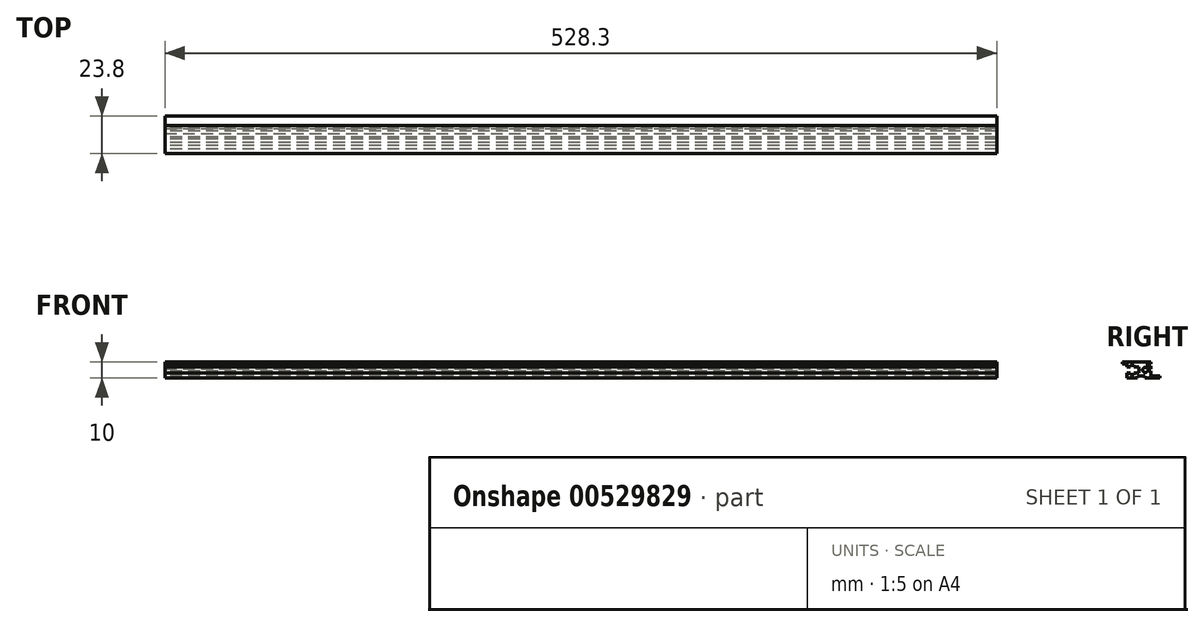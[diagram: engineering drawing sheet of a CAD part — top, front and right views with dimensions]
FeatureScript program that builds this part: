
annotation { "Feature Type Name" : "Feature", "Feature Type Description" : "" }
export const myFeature = defineFeature(function(context is Context, id is Id, definition is map)
    precondition{}
    {
        {
            assignVariable(context, id + "F0", {"name" : "length", "anyValue" : 528.3});
        }
        {
            var Q0;
            Q0=qCreatedBy(makeId("Right.planeOp"),FACE);
            var sketch = newSketch(context, id + "F1", { "sketchPlane" : qUnion([Q0])});
            skLineSegment(sketch, "E0.top", {"start": v(-37.38, 18.75) * mm, "end": v(-34.58, 18.75) * mm});
            skLineSegment(sketch, "E1", {"start": v(-37.38, 19.95) * mm, "end": v(-37.38, 18.75) * mm});
            skLineSegment(sketch, "E2.top", {"start": v(-13.58, 11.15) * mm, "end": v(-19.58, 11.15) * mm});
            skLineSegment(sketch, "E3", {"start": v(-37.38, 19.95) * mm, "end": v(-19.58, 19.95) * mm});
            skLineSegment(sketch, "E4", {"start": v(-13.58, 11.15) * mm, "end": v(-13.58, 9.95) * mm});
            skLineSegment(sketch, "E5.bottom", {"start": v(-19.58, 19.95) * mm, "end": v(-21.58, 19.95) * mm});
            skLineSegment(sketch, "E5.top", {"start": v(-19.58, 18.75) * mm, "end": v(-21.58, 18.75) * mm});
            skLineSegment(sketch, "E5.left", {"start": v(-19.58, 19.95) * mm, "end": v(-19.58, 18.75) * mm});
            skLineSegment(sketch, "E6.bottom", {"start": v(-21.58, 18.75) * mm, "end": v(-19.58, 18.75) * mm});
            skLineSegment(sketch, "E6.top", {"start": v(-21.58, 17.35) * mm, "end": v(-19.58, 17.35) * mm});
            skLineSegment(sketch, "E6.left", {"start": v(-21.58, 18.75) * mm, "end": v(-21.58, 17.35) * mm});
            skLineSegment(sketch, "E7.right", {"start": v(-26.98, 12.95) * mm, "end": v(-26.98, 16.95) * mm});
            skLineSegment(sketch, "E8", {"start": v(-34.58, 18.75) * mm, "end": v(-34.58, 16.95) * mm});
            skLineSegment(sketch, "E9.bottom", {"start": v(-34.58, 12.95) * mm, "end": v(-32.32, 12.95) * mm});
            skLineSegment(sketch, "E9.right", {"start": v(-32.32, 12.95) * mm, "end": v(-32.32, 11.7) * mm});
            skLineSegment(sketch, "E10.bottom", {"start": v(-32.32, 11.7) * mm, "end": v(-30.33, 11.7) * mm});
            skLineSegment(sketch, "E10.top", {"start": v(-32.32, 18.2) * mm, "end": v(-30.33, 18.2) * mm});
            skLineSegment(sketch, "E11", {"start": v(-34.58, 12.95) * mm, "end": v(-34.58, 9.95) * mm});
            skLineSegment(sketch, "E12", {"start": v(-34.58, 16.95) * mm, "end": v(-32.32, 16.95) * mm});
            skLineSegment(sketch, "E13", {"start": v(-26.98, 16.95) * mm, "end": v(-30.33, 16.95) * mm});
            skLineSegment(sketch, "E14", {"start": v(-32.32, 18.2) * mm, "end": v(-32.32, 16.95) * mm});
            skLineSegment(sketch, "E15", {"start": v(-26.98, 12.95) * mm, "end": v(-30.33, 12.95) * mm});
            skLineSegment(sketch, "E16", {"start": v(-30.33, 18.2) * mm, "end": v(-30.33, 16.95) * mm});
            skLineSegment(sketch, "E17", {"start": v(-30.33, 12.95) * mm, "end": v(-30.33, 11.7) * mm});
            skLineSegment(sketch, "E18.bottom", {"start": v(-19.58, 15.55) * mm, "end": v(-21.58, 15.55) * mm});
            skLineSegment(sketch, "E18.top", {"start": v(-19.58, 14.35) * mm, "end": v(-21.58, 14.35) * mm});
            skLineSegment(sketch, "E18.right", {"start": v(-21.58, 15.55) * mm, "end": v(-21.58, 14.35) * mm});
            skLineSegment(sketch, "E19", {"start": v(-19.58, 17.35) * mm, "end": v(-19.58, 15.55) * mm});
            skLineSegment(sketch, "E20", {"start": v(-19.58, 14.35) * mm, "end": v(-19.58, 11.15) * mm});
            skLineSegment(sketch, "E21.bottom", {"start": v(-13.58, 9.95) * mm, "end": v(-23.08, 9.95) * mm});
            skLineSegment(sketch, "E22.top", {"start": v(-23.08, 11.15) * mm, "end": v(-28.08, 11.15) * mm});
            skLineSegment(sketch, "E22.right", {"start": v(-28.08, 9.95) * mm, "end": v(-28.08, 11.15) * mm});
            skLineSegment(sketch, "E23", {"start": v(-34.58, 9.95) * mm, "end": v(-28.08, 9.95) * mm});
            skLineSegment(sketch, "E24", {"start": v(-23.08, 11.15) * mm, "end": v(-23.08, 9.95) * mm});
            skSolve(sketch);
        }
        {
            var Q0;
            Q0=qSketchRegion(id+"F1",true);
            extrude(context, id + "F2", {"entities" : qUnion([Q0]), "depth" : (getVariable(context, 'length')) * mm, "offsetDistance" : 25 * mm});
        }
        {
            var Q0;
            Q0=makeQuery(id+"F2.opExtrude","CAP_FACE",FACE,{"disambiguationData":[OSD([sQuery(id+"F1.wireOp",EDGE,"E0.top"),sQuery(id+"F1.wireOp",EDGE,"E0.right"),sQuery(id+"F1.wireOp",EDGE,"E1"),sQuery(id+"F1.wireOp",EDGE,"7WjtD8Os-DvTV-xx7e-wsHr-O7i4Oa3QZQYs"),sQuery(id+"F1.wireOp",EDGE,"E2.top"),sQuery(id+"F1.wireOp",EDGE,"E3"),sQuery(id+"F1.wireOp",EDGE,"E4"),sQuery(id+"F1.wireOp",EDGE,"E5.bottom"),sQuery(id+"F1.wireOp",EDGE,"E5.left"),sQuery(id+"F1.wireOp",EDGE,"E6.bottom"),sQuery(id+"F1.wireOp",EDGE,"E6.top"),sQuery(id+"F1.wireOp",EDGE,"E6.left"),sQuery(id+"F1.wireOp",EDGE,"5xcxBood-YYAR-WB05-Kpwu-UJQrYywPCwEj")])],"isStart":false});
            var sketch = newSketch(context, id + "F3", { "sketchPlane" : qUnion([Q0])});
            skCircle(sketch, "E25", {"center": v(-23.08, 14.95) * mm, "radius": 1.65 * mm});
            skSolve(sketch);
        }
        {
            var Q0;
            Q0=qSketchRegion(id+"F3",true);
            extrude(context, id + "F4", {"entities" : qUnion([Q0]), "operationType" : NewBodyOperationType.REMOVE, "oppositeDirection" : true, "depth" : (getVariable(context, 'length')) * mm, "offsetDistance" : 25 * mm});
        }
    });
